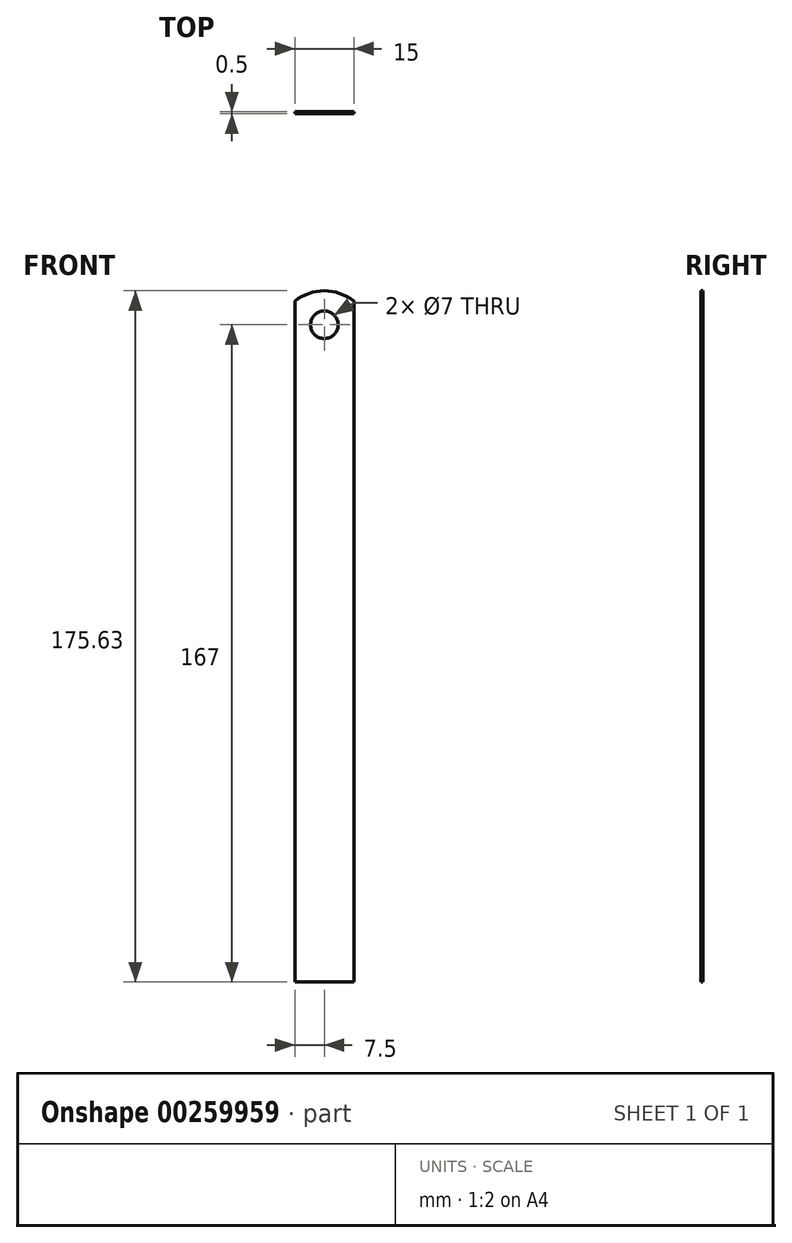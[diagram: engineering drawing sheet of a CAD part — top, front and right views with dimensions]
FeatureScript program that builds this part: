
annotation { "Feature Type Name" : "Feature", "Feature Type Description" : "" }
export const myFeature = defineFeature(function(context is Context, id is Id, definition is map)
    precondition{}
    {
        {
            var Q0;
            Q0=qCreatedBy(makeId("Front.planeOp"),FACE);
            var sketch = newSketch(context, id + "F0", { "sketchPlane" : qUnion([Q0])});
            skLineSegment(sketch, "E0", {"start": v(0, 0) * mm, "end": v(0, 173) * mm});
            skLineSegment(sketch, "E1", {"start": v(0, 173) * mm, "end": v(0, 0) * mm});
            skLineSegment(sketch, "E2", {"start": v(15, 0) * mm, "end": v(0, 0) * mm});
            skLineSegment(sketch, "E3", {"start": v(15, 173) * mm, "end": v(15, 0) * mm});
            skArc(sketch, "E4", {"start": v(15, 173) * mm, "mid": v(7.5, 175.63) * mm, "end": v(0, 173) * mm});
            skCircle(sketch, "E5", {"center": v(7.5, 167) * mm, "radius": 3.5 * mm});
            skLineSegment(sketch, "E6", {"start": v(7.5, 167) * mm, "end": v(7.5, 0) * mm, "construction": true});
            skPoint(sketch, "E7", {"position": v(7.5, 0) * mm});
            skSolve(sketch);
        }
        {
            var Q0;
            Q0 = qSketchRegion(id + "F0", true);
            extrude(context, id + "F1", {"entities" : qUnion([Q0]), "depth" : .5 * mm});
        }
    });
